# Revit family: Faucet-Kitchen-KOHLER-Coralais-K-15160
name_source: partatom
category: Plumbing Fixtures
revit_build: Autodesk Revit 2015 (Build: 20140606_1530(x64)
units: mm (PartAtom-declared; Revit-internal decimal feet)

## types (6) — shared parameters
ADA Compliant = Yes
Assembly Code = D2010
CW Connection = Yes
Cold Water Inlet = Cold Water Inlet
Date Modified = 02/11/2019
Default Elevation = 36"
Description = Single-hole or three-hole kitchen sink faucet with pull-out matching color sprayhead, 9 Inch spout reach and lever handle
Drain Included = No
Faucet Hole Spacing = 0"
Flow Rate = 2 GPM
HW Connection = Yes
Handle Clearance = 0"
Height = 8 3/8"
Hot Water Inlet = Hot Water Inlet
Length = 9"
Manufacturer = KOHLER Co.
MasterFormat 1995 = 15410
MasterFormat 2004 = 22.41.39
Material = Premium Metal Construction
Pressure = 60.00 psi
Product Documentation Link = https://www.us.kohler.com
Product Name = Coralais
Product Page URL = http://www.us.kohler.com
Spout Reach = 9"
URL = https://www.us.kohler.com
Vent Connection = No
Waste Connection = No
Waste Water Outlet = Waste Water Outlet
WaterSense Certified = No
Width = 10 1/2"

## per-type parameters (varying)
| type | Finish | Model | Type |
| CP-Polished Chrome | Kohler-Metal-CP-Polished_Chrome | K-15160-CP | 1 |
| G-Brushed Chrome | Kohler-Metal-G-Brushed_Chrome | K-15160-G | 2 |
| BN-Vibrant Brushed Nickel | Kohler-Metal-BN-Vibrant_Brushed_Nickel | K-15160-BN | 3 |
| 0-White | Kohler-Metal-0-White | K-15160-0 | 4 |
| 96-Biscuit | Kohler-Metal-96-Biscuit | K-15160-96 | 5 |
| 7-Black Black | Kohler-Metal-7-Black_Black | K-15160-7 | 6 |

## geometry (parser evidence)
native form markers: Sweep x7
no freeform markers — native parametric forms only
